# Revit family: Gira_039201
name_source: partatom
category: Electrical Fixtures
revit_build: Autodesk Revit 2017 (Build: 20160225_1515(x64)
units: mm (PartAtom-declared; Revit-internal decimal feet)

## family parameters
Cut with Voids When Loaded = No
Host = Face
Maintain Annotation Orientation = Yes
Part Type = Normal
Room Calculation Point = No
Round Connector Dimension = Use Diameter
Shared = No

## types (1)
- RTR 230/10 (4) A Öffner Aus + Kontroll System 55 Cremeweiß
    Anschluss = Zweidraht
    Art der Spannungsversorgung = 230V AC
    Ausführung = An/Aus
    Ausführung Aufnehmer/Fühler = sonstige
    Available = Yes
    Bedienung = Dreh
    Category = Raumthermostat
    Data sheet (1) = https://katalog.gira.de
    Default Elevation = 1219 mm
    Differenz verstellbar = No
    Explosionsgeschützt = No
    Farbe = cremeweiß
    GTIN = 4010337392019
    HAN = 039201
    HeinzeBIM = https://bimportal.heinze.de
    Heizen = Yes
    Kühlen = No
    Manufacturer URL = https://www.gira.de
    Messbereich oberer Wert = 30 m/s
    Messbereich unterer Wert = 5 m/s
    Mit Display = No
    Mit Empfänger = No
    Mit Geräuschniveauanzeige = No
    Mit Trinkwasserschaltung = No
    Model = Sys55_Komplettgerät_Schalten und Tasten
    Montageart = auf Putz
    Name = RTR 230/10 (4) A Öffner Aus + Kontroll System 55 Cremeweiß
    RAL-Nummer = 1013
    Regelcharakteristik = sonstige
    Region = DE
    Schutzart (IP) = IP20
    Sensor extern = No
    Temperatur ablesbar = No
    Thermische Rückkopplung = ohne
    Typ Kontakt = Öffner
    URL = http://katalog.gira.de

## geometry (parser evidence)
native form markers: Blend x2, Sweep x10
no freeform markers — native parametric forms only
